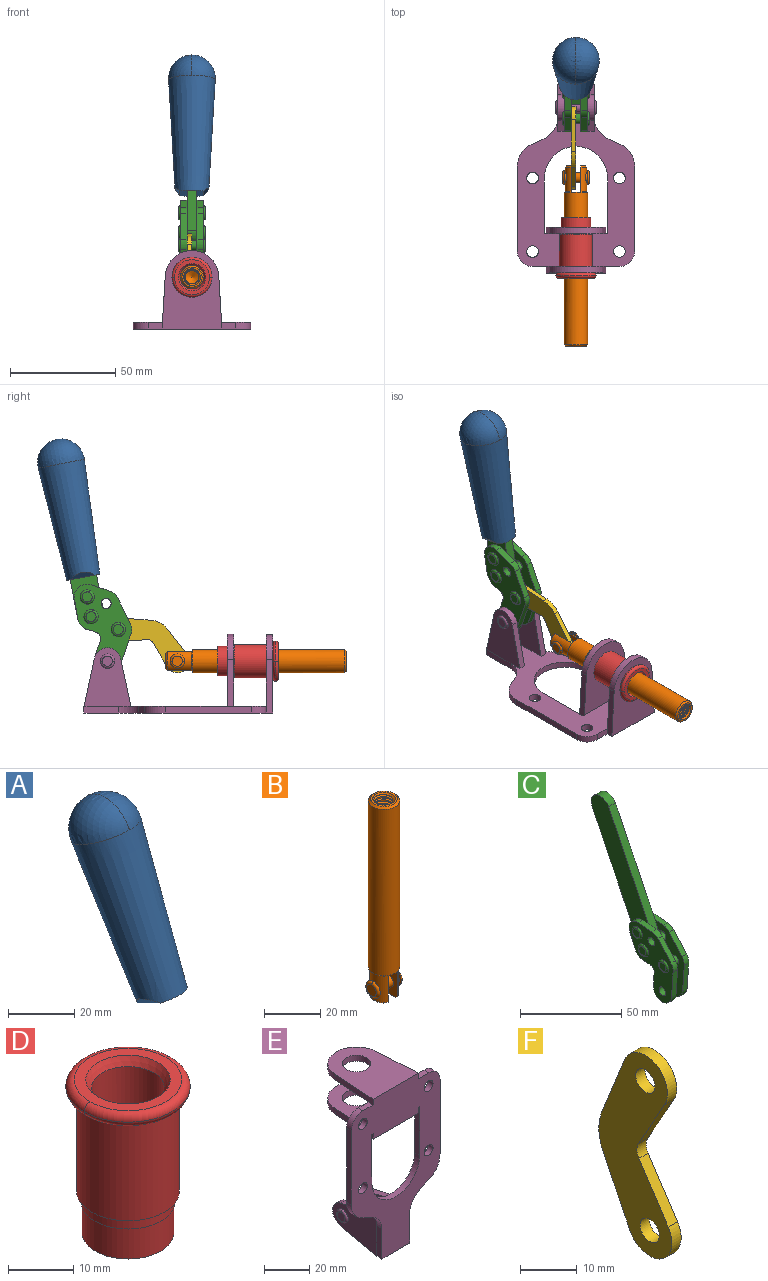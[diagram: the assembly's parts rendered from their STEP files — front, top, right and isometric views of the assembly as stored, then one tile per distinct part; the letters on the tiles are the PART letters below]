
ASSEMBLY  parts=6 mates=6
PART A: 11 faces, bbox 22.3x42.6x64.5 mm
  f0: sphere r=11.13mm, area 411.4mm2, adj f1,f8
  f1: cone r=11.11mm half-angle=3.3deg, axis (0,0.44,0.9), area 3251.8mm2, adj f0,f7,f8,f9,f10
  f2: cylinder r=6.16mm len=11.7mm, axis (1,0,0), area 89.5mm2, adj f3,f4,f5,f6
  f3: plane 60.23x36.75mm, normal (-1,0,0), area 763.6mm2, adj f2,f4,f6,f10
  f4: plane 51.37x25.05mm, normal (0,0.9,-0.44), area 264.2mm2, adj f2,f3,f5,f10
  f5: plane 60.23x36.75mm, normal (1,0,0), area 763.6mm2, adj f2,f4,f6,f10
  f6: plane 51.37x25.05mm, normal (0,-0.9,0.44), area 264.2mm2, adj f2,f3,f5,f10
  f7: plane 9.95x5.95mm, normal (0.71,-0.31,-0.64), area 25.8mm2, adj f1,f10
  f8: sphere r=11.13mm, area 411.4mm2, adj f0,f1
  f9: plane 9.95x5.95mm, normal (-0.71,-0.31,-0.64), area 25.8mm2, adj f1,f10
  f10: plane 14.27x11.38mm, normal (0,-0.44,-0.9), area 106.7mm2, adj f1,f3,f4,f5,f6,f7,f9
PART B: 48 faces, bbox 12.6x11.1x86.1 mm
  f0: torus R=2.41mm, axis (-1,0,0), area 15mm2, adj f30,f32,f34
  f1: torus R=2.41mm, axis (-1,0,0), area 15mm2, adj f29,f31,f33
  f2: cylinder r=5.54mm len=72.39mm, axis (0,0,1), area 2518.5mm2, adj f3,f4,f42,f43
  f3: cone r=5.54mm half-angle=45deg, axis (0,0,1), area 7.6mm2, adj f2,f5,f41
  f4: cone r=5.54mm half-angle=45deg, axis (0,0,-1), area 34.9mm2, adj f2,f39
  f5: cylinder r=5.08mm len=11.48mm, axis (0,0,1), area 108.3mm2, adj f3,f7,f8,f41
  f6: cylinder r=2.41mm len=4.83mm, axis (-1,0,0), area 71.2mm2, adj f40,f41
  f7: cylinder r=2.41mm len=4.83mm, axis (-1,0,0), area 7.6mm2, adj f5,f34
  f8: cone r=5.08mm half-angle=45deg, axis (0,0,1), area 10.6mm2, adj f5,f37,f41
  f9: cone r=3.98mm half-angle=45deg, axis (0,0,1), area 17.6mm2, adj f27,f39,f45,f46,f47
  f10: cylinder r=2.41mm len=4.83mm, axis (-1,0,0), area 7.6mm2, adj f33,f38
  f11: cylinder r=3.2mm len=6.4mm, axis (0,0,1), area 78.4mm2, adj f12,f28,f44,f45,f47
  f12: cylinder r=3.2mm len=6.4mm, axis (0,0,1), area 10.5mm2, adj f11,f13,f45,f47
  f13: cylinder r=3.2mm len=6.4mm, axis (0,0,1), area 10.5mm2, adj f12,f14,f45,f47
  f14: cylinder r=3.2mm len=6.4mm, axis (0,0,1), area 10.5mm2, adj f13,f15,f45,f47
  f15: cylinder r=3.2mm len=6.4mm, axis (0,0,1), area 10.5mm2, adj f14,f16,f45,f47
  f16: cylinder r=3.2mm len=6.4mm, axis (0,0,1), area 10.5mm2, adj f15,f17,f45,f47
  f17: cylinder r=3.2mm len=6.4mm, axis (0,0,1), area 10.5mm2, adj f16,f18,f45,f47
  f18: cylinder r=3.2mm len=6.4mm, axis (0,0,1), area 10.5mm2, adj f17,f19,f45,f47
  f19: cylinder r=3.2mm len=6.4mm, axis (0,0,1), area 10.5mm2, adj f18,f20,f45,f47
  f20: cylinder r=3.2mm len=6.4mm, axis (0,0,1), area 10.5mm2, adj f19,f21,f45,f47
  f21: cylinder r=3.2mm len=6.4mm, axis (0,0,1), area 10.5mm2, adj f20,f22,f45,f47
  f22: cylinder r=3.2mm len=6.4mm, axis (0,0,1), area 10.5mm2, adj f21,f23,f45,f47
  f23: cylinder r=3.2mm len=6.4mm, axis (0,0,1), area 10.5mm2, adj f22,f24,f45,f47
  f24: cylinder r=3.2mm len=6.4mm, axis (0,0,1), area 10.5mm2, adj f23,f25,f45,f47
  f25: cylinder r=3.2mm len=6.4mm, axis (0,0,1), area 10.5mm2, adj f24,f26,f45,f47
  f26: cylinder r=3.2mm len=6.4mm, axis (0,0,1), area 10.5mm2, adj f25,f27,f45,f47
  f27: cylinder r=3.2mm len=6.4mm, axis (0,0,1), area 7.4mm2, adj f9,f26,f45,f47
  f28: cone r=3.2mm half-angle=60deg, axis (0,0,1), area 37.2mm2, adj f11
  f29: plane 4.83x4.83mm, normal (-1,0,0), area 18.3mm2, adj f1,f31
  f30: plane 4.83x4.83mm, normal (1,0,0), area 18.3mm2, adj f0,f32
  f31: torus R=2.41mm, axis (-1,0,0), area 15mm2, adj f1,f29,f33
  f32: torus R=2.41mm, axis (-1,0,0), area 15mm2, adj f0,f30,f34
  f33: plane 6.83x6.83mm, normal (1,0,0), area 18.3mm2, adj f1,f10,f31
  f34: plane 6.83x6.83mm, normal (-1,0,0), area 18.3mm2, adj f0,f7,f32
  f35: cone r=5.08mm half-angle=45deg, axis (0,0,1), area 10.6mm2, adj f36,f38,f40
  f36: plane 7.25x1.97mm, normal (0,0,-1), area 10mm2, adj f35,f40
  f37: plane 7.25x1.97mm, normal (0,0,-1), area 10mm2, adj f8,f41
  f38: cylinder r=5.08mm len=11.48mm, axis (0,0,1), area 108.3mm2, adj f10,f35,f40,f42
  f39: plane 9.55x9.55mm, normal (0,0,1), area 22mm2, adj f4,f9
  f40: plane 12.76x10.09mm, normal (1,0,0), area 95.7mm2, adj f6,f35,f36,f38,f42,f43
  f41: plane 12.76x10.09mm, normal (-1,0,0), area 95.7mm2, adj f3,f5,f6,f8,f37,f43
  f42: cone r=5.54mm half-angle=45deg, axis (0,0,1), area 7.6mm2, adj f2,f38,f40
  f43: plane 11.07x4.7mm, normal (0,0,-1), area 50.4mm2, adj f2,f40,f41
  f44: plane 0.89x0.62mm, normal (-1,0,0), area 0.3mm2, adj f11,f45,f46,f47
  f45: bspline ~24.8x7.63mm, area 266.6mm2, adj f9,f11,f12,f13,f14,f15,f16,f17
  f46: bspline ~24.87x7.63mm, area 73.6mm2, adj f9,f44,f45,f47
  f47: bspline ~24.98x7.63mm, area 272.5mm2, adj f9,f11,f12,f13,f14,f15,f16,f17
PART C: 59 faces, bbox 12.9x60.2x99.6 mm
  f0: torus R=2.39mm, axis (-1,0,0), area 14.9mm2, adj f20,f43,f51
  f1: torus R=2.39mm, axis (-1,0,0), area 14.9mm2, adj f19,f42,f51
  f2: torus R=2.39mm, axis (-1,0,0), area 14.9mm2, adj f18,f35,f51
  f3: torus R=2.39mm, axis (-1,0,0), area 14.9mm2, adj f14,f17,f23
  f4: torus R=2.39mm, axis (-1,0,0), area 14.9mm2, adj f13,f16,f23
  f5: torus R=2.39mm, axis (-1,0,0), area 14.9mm2, adj f12,f15,f23
  f6: cylinder r=2.39mm len=4.78mm, axis (1,0,0), area 46.5mm2, adj f48,f50,f51
  f7: cylinder r=2.39mm len=4.78mm, axis (1,0,0), area 46.5mm2, adj f50,f51
  f8: cylinder r=6.35mm len=12.68mm, axis (1,0,0), area 61.8mm2, adj f38,f39,f50,f51
  f9: cylinder r=2.39mm len=4.78mm, axis (-1,0,0), area 70.5mm2, adj f46,f50
  f10: cylinder r=2.39mm len=4.78mm, axis (-1,0,0), area 46.5mm2, adj f23,f45,f46
  f11: cylinder r=2.39mm len=4.78mm, axis (-1,0,0), area 46.5mm2, adj f23,f46
  f12: plane 4.78x4.78mm, normal (1,0,0), area 17.9mm2, adj f5,f15
  f13: plane 4.78x4.78mm, normal (1,0,0), area 17.9mm2, adj f4,f16
  f14: plane 4.78x4.78mm, normal (1,0,0), area 17.9mm2, adj f3,f17
  f15: torus R=2.39mm, axis (-1,0,0), area 14.9mm2, adj f5,f12,f23
  f16: torus R=2.39mm, axis (-1,0,0), area 14.9mm2, adj f4,f13,f23
  f17: torus R=2.39mm, axis (-1,0,0), area 14.9mm2, adj f3,f14,f23
  f18: plane 4.78x4.78mm, normal (-1,0,0), area 17.9mm2, adj f2,f35
  f19: plane 4.78x4.78mm, normal (-1,0,0), area 17.9mm2, adj f1,f42
  f20: plane 4.78x4.78mm, normal (-1,0,0), area 17.9mm2, adj f0,f43
  f21: plane 2.26x0.2mm, normal (1,0,0), area 0.2mm2, adj f31,f44
  f22: plane 2.26x0.2mm, normal (-1,0,0), area 0.2mm2, adj f41,f44
  f23: plane 39.37x30.77mm, normal (1,0,0), area 565.5mm2, adj f3,f4,f5,f10,f11,f15,f16,f17
  f24: cylinder r=6.1mm len=4.15mm, axis (-1,0,0), area 14.7mm2, adj f23,f25,f32,f46
  f25: plane 10.25x9.01mm, normal (0,-0.75,0.66), area 42.3mm2, adj f23,f24,f26,f46
  f26: cylinder r=6.35mm len=4.64mm, axis (-1,0,0), area 15.6mm2, adj f23,f25,f27,f46
  f27: plane 15.84x3.1mm, normal (0,-1,-0.07), area 49.2mm2, adj f23,f26,f28,f46
  f28: cylinder r=6.35mm len=12.68mm, axis (-1,0,0), area 61.8mm2, adj f23,f27,f29,f46
  f29: plane 8.11x3.1mm, normal (0,1,0.07), area 25.2mm2, adj f23,f28,f30,f46
  f30: cylinder r=3.05mm len=3.25mm, axis (-1,0,0), area 14.8mm2, adj f23,f29,f31,f46
  f31: plane 5.99x3.1mm, normal (0,0.07,-1), area 18.6mm2, adj f21,f23,f30,f44,f46
  f32: plane 9.5x3.1mm, normal (0,-0.07,1), area 29.5mm2, adj f23,f24,f33,f46,f47
  f33: cylinder r=6.1mm len=8.63mm, axis (-1,0,0), area 39.1mm2, adj f23,f32,f34,f47
  f34: plane 8.65x3.96mm, normal (0,0.91,-0.42), area 29.5mm2, adj f23,f33,f44,f47
  f35: torus R=2.39mm, axis (-1,0,0), area 14.9mm2, adj f2,f18,f51
  f36: plane 10.25x9.01mm, normal (0,-0.75,0.66), area 42.3mm2, adj f37,f49,f50,f51
  f37: cylinder r=6.35mm len=4.64mm, axis (1,0,0), area 15.6mm2, adj f36,f38,f50,f51
  f38: plane 15.84x3.1mm, normal (0,-1,-0.07), area 49.2mm2, adj f8,f37,f50,f51
  f39: plane 8.11x3.1mm, normal (0,1,0.07), area 25.2mm2, adj f8,f40,f50,f51
  f40: cylinder r=3.05mm len=3.25mm, axis (1,0,0), area 14.8mm2, adj f39,f41,f50,f51
  f41: plane 5.99x3.1mm, normal (0,0.07,-1), area 18.6mm2, adj f22,f40,f44,f50,f51
  f42: torus R=2.39mm, axis (-1,0,0), area 14.9mm2, adj f1,f19,f51
  f43: torus R=2.39mm, axis (-1,0,0), area 14.9mm2, adj f0,f20,f51
  f44: cylinder r=6.35mm len=12.12mm, axis (-1,0,0), area 128.9mm2, adj f21,f22,f23,f31,f34,f41,f46,f47
  f45: plane 2.65x1.35mm, normal (1,0,0), area 1mm2, adj f10,f55
  f46: plane 39.08x20.42mm, normal (-1,0,0), area 412.5mm2, adj f9,f10,f11,f24,f25,f26,f27,f28
  f47: plane 77.62x39.82mm, normal (1,0,0), area 850mm2, adj f32,f33,f34,f44,f53,f54,f55
  f48: plane 2.65x1.35mm, normal (-1,0,0), area 1mm2, adj f6,f55
  f49: cylinder r=6.1mm len=4.15mm, axis (1,0,0), area 14.7mm2, adj f36,f50,f51,f56
  f50: plane 39.08x20.42mm, normal (1,0,0), area 412.5mm2, adj f6,f7,f8,f9,f36,f37,f38,f39
  f51: plane 39.37x30.77mm, normal (-1,0,0), area 565.5mm2, adj f0,f1,f2,f6,f7,f8,f35,f36
  f52: plane 8.65x3.96mm, normal (0,0.91,-0.42), area 29.5mm2, adj f44,f51,f57,f58
  f53: plane 68.49x33.4mm, normal (0,0.9,-0.44), area 358.1mm2, adj f44,f47,f54,f58
  f54: cylinder r=6.35mm len=12.06mm, axis (1,0,0), area 93.7mm2, adj f47,f53,f55,f58
  f55: plane 68.49x33.4mm, normal (0,-0.9,0.44), area 358.1mm2, adj f44,f45,f46,f47,f48,f50,f54,f58
  f56: plane 9.5x3.1mm, normal (0,-0.07,1), area 29.5mm2, adj f49,f50,f51,f57,f58
  f57: cylinder r=6.1mm len=8.63mm, axis (1,0,0), area 39.1mm2, adj f51,f52,f56,f58
  f58: plane 77.62x39.82mm, normal (-1,0,0), area 850mm2, adj f44,f52,f53,f54,f55,f56,f57
PART D: 15 faces, bbox 20.6x20.6x28.7 mm
  f0: torus R=8.26mm, axis (0,0,1), area 56.8mm2, adj f1,f10,f12
  f1: torus R=8.26mm, axis (0,0,1), area 56.8mm2, adj f0,f6,f13
  f2: cylinder r=5.59mm len=25.91mm, axis (0,0,1), area 909.6mm2, adj f3,f4
  f3: cone r=6.86mm half-angle=45deg, axis (0,0,-1), area 70.2mm2, adj f2,f14
  f4: cone r=6.47mm half-angle=30deg, axis (0,0,1), area 66.7mm2, adj f2,f13
  f5: cylinder r=7.04mm len=14.07mm, axis (0,0,1), area 252.6mm2, adj f11,f14
  f6: torus R=8.26mm, axis (0,0,1), area 56.8mm2, adj f1,f12,f13
  f7: cylinder r=7.16mm len=14.33mm, axis (0,0,1), area 91.5mm2, adj f9,f11
  f8: cylinder r=7.86mm len=18.42mm, axis (0,0,1), area 909.6mm2, adj f9,f10
  f9: plane 15.72x15.72mm, normal (0,0,-1), area 33mm2, adj f7,f8
  f10: plane 16.51x16.51mm, normal (0,0,-1), area 19.9mm2, adj f0,f8,f12
  f11: plane 14.33x14.33mm, normal (0,0,-1), area 5.7mm2, adj f5,f7
  f12: torus R=8.26mm, axis (0,0,1), area 56.8mm2, adj f0,f6,f10
  f13: plane 16.51x16.51mm, normal (0,0,1), area 82.7mm2, adj f1,f4,f6
  f14: plane 14.07x14.07mm, normal (0,0,-1), area 7.8mm2, adj f3,f5
PART E: 55 faces, bbox 55.7x37.4x89.8 mm
  f0: torus R=2.41mm, axis (-1,0,0), area 15mm2, adj f11,f15,f25
  f1: torus R=2.41mm, axis (-1,0,0), area 15mm2, adj f10,f12,f22
  f2: cylinder r=2.78mm len=5.56mm, axis (0,-1,0), area 54.2mm2, adj f30,f54
  f3: cylinder r=14.99mm len=29.97mm, axis (0,-1,0), area 145.9mm2, adj f30,f49,f53,f54
  f4: cylinder r=2.78mm len=5.56mm, axis (0,-1,0), area 54.2mm2, adj f30,f54
  f5: cylinder r=2.78mm len=5.56mm, axis (0,-1,0), area 54.2mm2, adj f30,f54
  f6: cylinder r=2.78mm len=5.56mm, axis (0,-1,0), area 54.2mm2, adj f30,f54
  f7: cylinder r=6.35mm len=12.7mm, axis (0,0,1), area 123.6mm2, adj f27,f51
  f8: cylinder r=6.35mm len=12.7mm, axis (0,0,-1), area 124.7mm2, adj f21,f35
  f9: cylinder r=2.41mm len=11.18mm, axis (-1,0,0), area 169.4mm2, adj f16,f19
  f10: plane 4.83x4.83mm, normal (1,0,0), area 18.3mm2, adj f1,f12
  f11: plane 4.83x4.83mm, normal (-1,0,0), area 18.3mm2, adj f0,f15
  f12: torus R=2.41mm, axis (-1,0,0), area 15mm2, adj f1,f10,f22
  f13: cylinder r=6.35mm len=12.41mm, axis (1,0,0), area 53.4mm2, adj f18,f19,f22,f23
  f14: cylinder r=6.35mm len=12.41mm, axis (-1,0,0), area 53.4mm2, adj f16,f17,f24,f25
  f15: torus R=2.41mm, axis (-1,0,0), area 15mm2, adj f0,f11,f25
  f16: plane 27.86x22.35mm, normal (1,0,0), area 425.4mm2, adj f9,f14,f17,f24,f30
  f17: plane 22.86x4.97mm, normal (0,0.21,0.98), area 72.5mm2, adj f14,f16,f25,f30
  f18: plane 22.86x4.97mm, normal (0,0.21,0.98), area 72.5mm2, adj f13,f19,f22,f30
  f19: plane 27.86x22.35mm, normal (-1,0,0), area 425.4mm2, adj f9,f13,f18,f23,f30
  f20: cylinder r=12.7mm len=25.35mm, axis (0,0,-1), area 119.8mm2, adj f21,f34,f35,f36
  f21: plane 34.21x28.07mm, normal (0,0,-1), area 702.4mm2, adj f8,f20,f30,f34,f36
  f22: plane 27.96x22.45mm, normal (1,0,0), area 407.2mm2, adj f1,f12,f13,f18,f23,f30,f42,f43
  f23: plane 22.86x4.97mm, normal (0,0.21,-0.98), area 72.5mm2, adj f13,f19,f22,f44
  f24: plane 22.86x4.97mm, normal (0,0.21,-0.98), area 72.5mm2, adj f14,f16,f25,f44
  f25: plane 27.86x22.35mm, normal (-1,0,0), area 407.1mm2, adj f0,f14,f15,f17,f24,f30,f45,f46
  f26: plane 3.1x0.95mm, normal (0,0,-1), area 2.7mm2, adj f30,f49,f50,f54
  f27: plane 34.21x28.07mm, normal (0,0,1), area 702.4mm2, adj f7,f28,f30,f50,f52
  f28: cylinder r=12.7mm len=25.35mm, axis (0,0,1), area 118.8mm2, adj f27,f50,f51,f52
  f29: plane 3.1x0.95mm, normal (0,0,-1), area 2.7mm2, adj f30,f52,f53,f54
  f30: plane 86.54x55.63mm, normal (0,1,0), area 2362.9mm2, adj f2,f3,f4,f5,f6,f16,f17,f18
  f31: plane 40.56x3.1mm, normal (-1,0,0), area 125.7mm2, adj f30,f32,f48,f54
  f32: cylinder r=7.11mm len=7.11mm, axis (0,-1,0), area 34.6mm2, adj f30,f31,f33,f54
  f33: plane 6.67x3.1mm, normal (0,0,1), area 20.4mm2, adj f30,f32,f34,f54
  f34: plane 25.39x3.13mm, normal (-1,0.06,0), area 79.5mm2, adj f20,f21,f33,f35,f54
  f35: plane 37.31x28.45mm, normal (0,0,1), area 789.9mm2, adj f8,f20,f34,f36,f54
  f36: plane 25.39x3.13mm, normal (1,0.06,0), area 79.5mm2, adj f20,f21,f35,f37,f54
  f37: plane 6.67x3.1mm, normal (0,0,1), area 20.4mm2, adj f30,f36,f38,f54
  f38: cylinder r=7.11mm len=7.11mm, axis (0,-1,0), area 34.6mm2, adj f30,f37,f39,f54
  f39: plane 40.56x3.1mm, normal (1,0,0), area 125.7mm2, adj f30,f38,f40,f54
  f40: cylinder r=11.18mm len=10.16mm, axis (0,-1,0), area 39.5mm2, adj f30,f39,f41,f54
  f41: plane 6.09x3.1mm, normal (0.42,0,-0.91), area 20.8mm2, adj f30,f40,f42,f54
  f42: cylinder r=11.18mm len=9.41mm, axis (0,-1,0), area 37.2mm2, adj f22,f30,f41,f43,f54
  f43: plane 16.5x3.1mm, normal (1,0,0), area 51.1mm2, adj f22,f42,f44,f54
  f44: plane 17.37x3.1mm, normal (0,0,-1), area 53.8mm2, adj f23,f24,f30,f43,f45,f54
  f45: plane 16.5x3.1mm, normal (-1,0,0), area 51.1mm2, adj f25,f44,f46,f54
  f46: cylinder r=11.18mm len=9.41mm, axis (0,-1,0), area 37.2mm2, adj f25,f30,f45,f47,f54
  f47: plane 6.09x3.1mm, normal (-0.42,0,-0.91), area 20.8mm2, adj f30,f46,f48,f54
  f48: cylinder r=11.18mm len=10.16mm, axis (0,-1,0), area 39.5mm2, adj f30,f31,f47,f54
  f49: plane 26.54x3.1mm, normal (-1,0,0), area 82.3mm2, adj f3,f26,f30,f54
  f50: plane 25.39x3.1mm, normal (1,0.06,0), area 78.8mm2, adj f26,f27,f28,f51,f54
  f51: plane 37.31x28.45mm, normal (0,0,-1), area 789.9mm2, adj f7,f28,f50,f52,f54
  f52: plane 25.39x3.1mm, normal (-1,0.06,0), area 78.8mm2, adj f27,f28,f29,f51,f54
  f53: plane 26.54x3.1mm, normal (1,0,0), area 82.3mm2, adj f3,f29,f30,f54
  f54: plane 89.66x55.63mm, normal (0,-1,0), area 2678.5mm2, adj f2,f3,f4,f5,f6,f26,f29,f31
PART F: 12 faces, bbox 2.3x18.2x42.8 mm
  f0: cylinder r=2.4mm len=4.8mm, axis (1,0,0), area 34.9mm2, adj f4,f11
  f1: cylinder r=10.41mm len=8.47mm, axis (1,0,0), area 20.2mm2, adj f4,f9,f10,f11
  f2: cylinder r=3.05mm len=3.16mm, axis (1,0,0), area 7.7mm2, adj f4,f6,f7,f11
  f3: cylinder r=2.4mm len=4.8mm, axis (1,0,0), area 34.9mm2, adj f4,f11
  f4: plane 42.81x18.23mm, normal (-1,0,0), area 414.1mm2, adj f0,f1,f2,f3,f5,f6,f7,f8
  f5: cylinder r=5.54mm len=10.67mm, axis (1,0,0), area 41.8mm2, adj f4,f6,f10,f11
  f6: plane 11.66x6.53mm, normal (0,-0.87,-0.49), area 30.9mm2, adj f2,f4,f5,f11
  f7: plane 11.17x7.33mm, normal (0,-0.84,0.55), area 30.9mm2, adj f2,f4,f8,f11
  f8: cylinder r=5.54mm len=10.51mm, axis (1,0,0), area 41.8mm2, adj f4,f7,f9,f11
  f9: plane 13.67x6.67mm, normal (0,0.9,-0.44), area 35.1mm2, adj f1,f4,f8,f11
  f10: plane 14.1x5.7mm, normal (0,0.93,0.37), area 35.1mm2, adj f1,f4,f5,f11
  f11: plane 42.81x18.23mm, normal (1,0,0), area 414.1mm2, adj f0,f1,f2,f3,f5,f6,f7,f8
PLACE A rot(axis=(1,0,0),15deg) t=(-0.04,9.15,49.24)mm
PLACE B rot(axis=(1,0,0),90deg) t=(0,23.56,0)mm
PLACE C rot(axis=(1,0,0),15deg) t=(0,9.15,49.24)mm
PLACE D rot(axis=(1,0,0),90deg) t=(0,9.14,0)mm
PLACE E rot(axis=(1,0,0),90deg) t=(0,9.14,0)mm fixed
PLACE F rot(axis=(1,0,0),120.2deg) t=(-1.16,33.84,11.13)mm
MATE revolute C.f7 <-> E.f0  axis (-1,0,0) through (0,41.23,24.61)mm
MATE fastened D.f2 <-> E.f7  axis (0,-1,0) through (0,-37.25,24.61)mm
MATE fastened A.f2 <-> C.f54  axis (1,0,0) through (-2.35,63.6,120.54)mm
MATE revolute F.f5 <-> B.f6  axis (-1,0,0) through (0,8.09,24.61)mm
MATE revolute F.f3 <-> C.f4  axis (-1,0,0) through (0,36.06,39.62)mm
MATE slider E.f7 <-> B.f2  axis (0,-1,0) through (0,-37.25,24.61)mm
